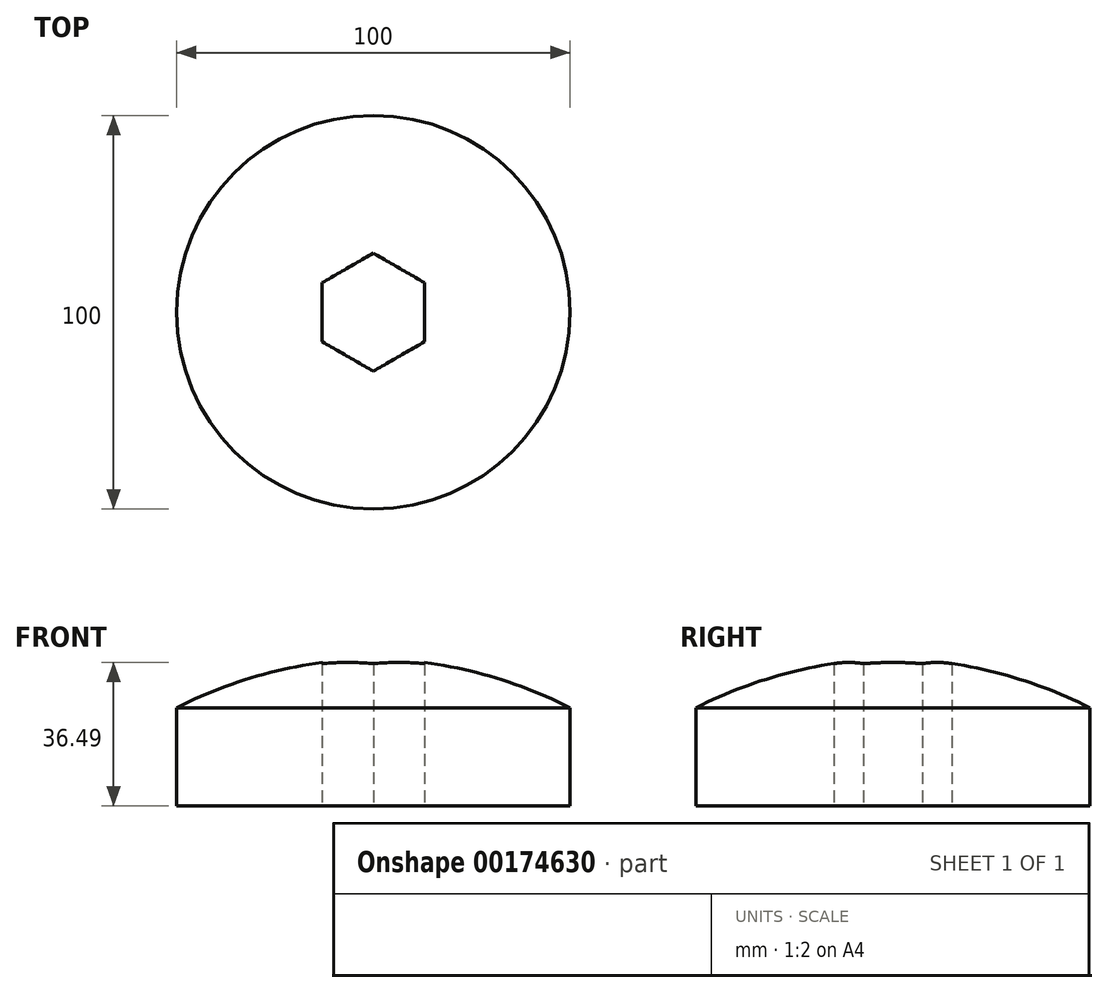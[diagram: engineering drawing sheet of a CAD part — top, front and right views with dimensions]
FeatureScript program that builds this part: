
annotation { "Feature Type Name" : "Feature", "Feature Type Description" : "" }
export const myFeature = defineFeature(function(context is Context, id is Id, definition is map)
    precondition{}
    {
        {
            var Q0;
            Q0=qCreatedBy(makeId("Top.planeOp"),FACE);
            var sketch = newSketch(context, id + "F0", { "sketchPlane" : qUnion([Q0])});
            skCircle(sketch, "E0", {"center": v(0, 0) * mm, "radius": 50 * mm});
            skCircle(sketch, "E1.cCircle", {"center": v(0, 0) * mm, "radius": 15 * mm, "construction": true});
            skLineSegment(sketch, "E1.0", {"start": v(0, 15) * mm, "end": v(13, 7.5) * mm});
            skLineSegment(sketch, "E1.1", {"start": v(13, 7.5) * mm, "end": v(13, -7.5) * mm});
            skLineSegment(sketch, "E1.2", {"start": v(13, -7.5) * mm, "end": v(0, -15) * mm});
            skLineSegment(sketch, "E1.3", {"start": v(0, -15) * mm, "end": v(-13, -7.5) * mm});
            skLineSegment(sketch, "E1.4", {"start": v(-13, -7.5) * mm, "end": v(-13, 7.5) * mm});
            skLineSegment(sketch, "E1.5", {"start": v(-13, 7.5) * mm, "end": v(0, 15) * mm});
            skSolve(sketch);
        }
        {
            var Q0;
            Q0=makeQuery(id+"F0.imprint","IMPRINT",FACE,{"disambiguationData":[TD([[makeQuery(id+"F0.imprint","IMPRINT",EDGE,{"derivedFrom":sQuery(id+"F0.wireOp",EDGE,"E0")}),1.0]])]});
            extrude(context, id + "F1", {"entities" : qUnion([Q0]), "depth" : 25 * mm});
        }
        {
            var Q0;
            Q0=qCreatedBy(makeId("Front.planeOp"),FACE);
            var sketch = newSketch(context, id + "F2", { "sketchPlane" : qUnion([Q0])});
            skLineSegment(sketch, "E2", {"start": v(0, 25) * mm, "end": v(0, 37.48) * mm, "construction": true});
            skArc(sketch, "E3", {"start": v(50, 25) * mm, "mid": v(25.7, 34.06) * mm, "end": v(0, 37.48) * mm});
            skPoint(sketch, "E4.orphan", {"position": v(50, 25) * mm});
            skPoint(sketch, "E5.0.start.orphan", {"position": v(-50, 25) * mm});
            skLineSegment(sketch, "E6", {"start": v(0, 37.48) * mm, "end": v(0, 25) * mm});
            skLineSegment(sketch, "E7", {"start": v(50, 25) * mm, "end": v(0, 25) * mm});
            skSolve(sketch);
        }
        {
            var Q0;
            Q0 = qSketchRegion(id + "F2", true);
            var Q1;
            Q1=sQuery(id+"F2.wireOp",EDGE,"E3");
            var Q2;
            Q2=sQuery(id+"F2.wireOp",EDGE,"E2");
            revolve(context, id + "F3", {"operationType" : NewBodyOperationType.ADD, "entities" : qUnion([Q0]), "surfaceEntities" : qUnion([Q1]), "axis" : qUnion([Q2]), "revolveType" : RevolveType.FULL});
        }
        {
            var Q0;
            Q0=makeQuery(id+"F3.opRevolve","SWEPT_FACE",FACE,{"disambiguationData":[OSD([sQuery(id+"F2.wireOp",EDGE,"E7")])]});
            extrude(context, id + "F4", {"entities" : qUnion([Q0]), "operationType" : NewBodyOperationType.REMOVE, "endBound" : BoundingType.THROUGH_ALL, "oppositeDirection" : true, "depth" : 25 * mm});
        }
    });
